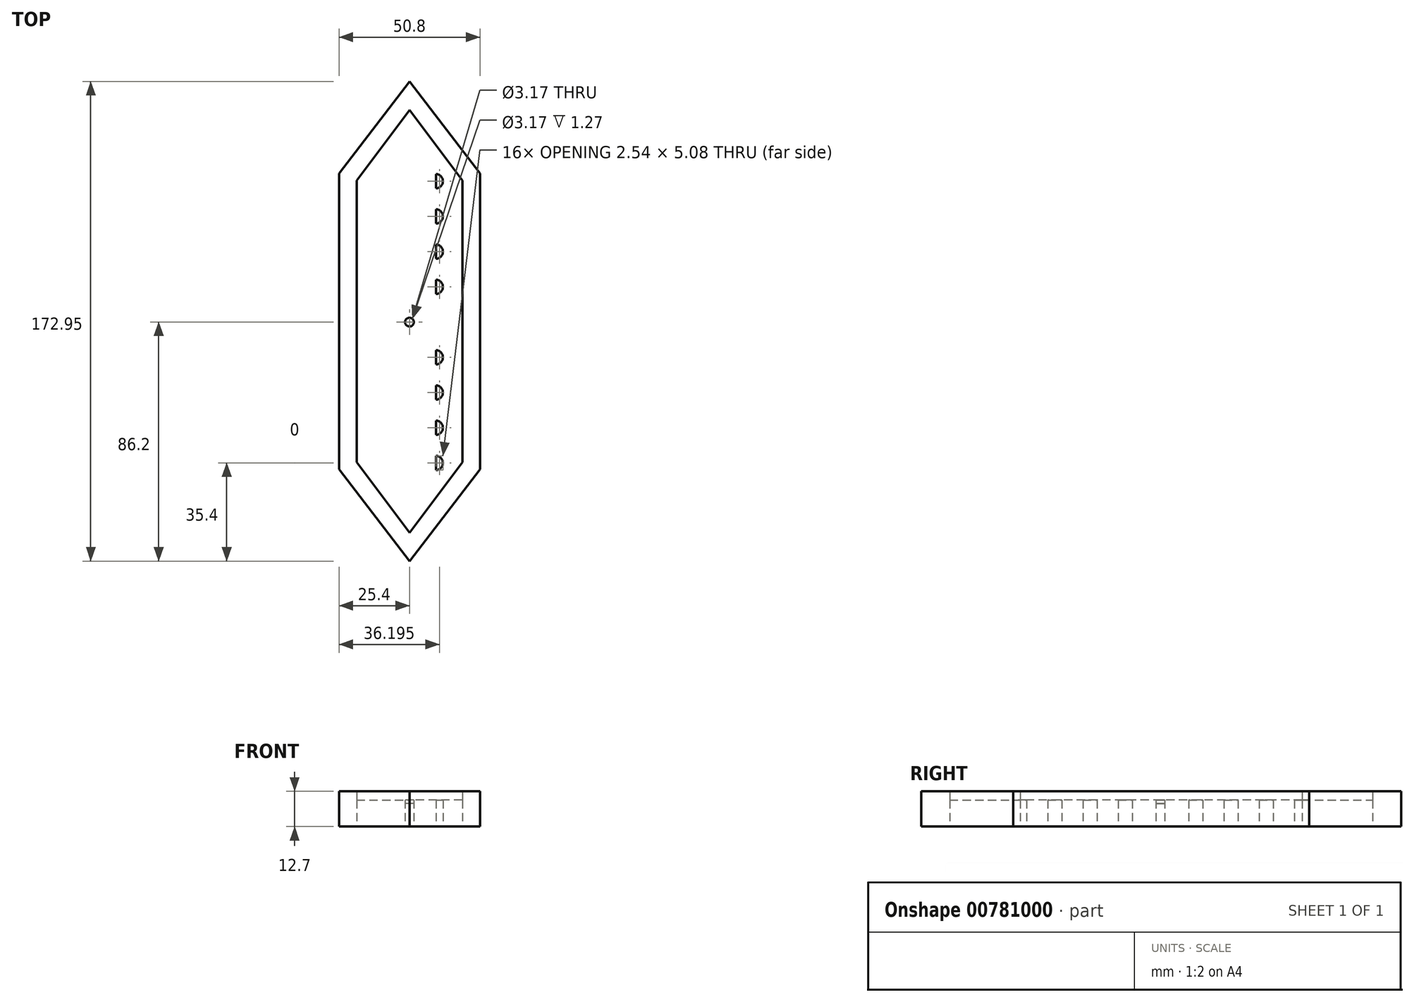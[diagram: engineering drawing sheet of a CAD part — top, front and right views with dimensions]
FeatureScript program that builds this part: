
annotation { "Feature Type Name" : "Feature", "Feature Type Description" : "" }
export const myFeature = defineFeature(function(context is Context, id is Id, definition is map)
    precondition{}
    {
        {
            var Q0;
            Q0=qCreatedBy(makeId("Top.planeOp"),FACE);
            var sketch = newSketch(context, id + "F0", { "sketchPlane" : qUnion([Q0])});
            skLineSegment(sketch, "E0", {"start": v(-25.4, 53.61) * mm, "end": v(-25.4, -53.07) * mm});
            skLineSegment(sketch, "E1", {"start": v(-25.4, -53.07) * mm, "end": v(0, -86.2) * mm});
            skLineSegment(sketch, "E2", {"start": v(0, -86.2) * mm, "end": v(25.4, -53.07) * mm});
            skLineSegment(sketch, "E3", {"start": v(25.4, -53.07) * mm, "end": v(25.4, 53.61) * mm});
            skLineSegment(sketch, "E4", {"start": v(25.4, 53.61) * mm, "end": v(0, 86.75) * mm});
            skLineSegment(sketch, "E5", {"start": v(0, 86.75) * mm, "end": v(-25.4, 53.61) * mm});
            skLineSegment(sketch, "E6", {"start": v(-19.05, 51.07) * mm, "end": v(0, 76.47) * mm});
            skLineSegment(sketch, "E7", {"start": v(0, 76.47) * mm, "end": v(19.05, 51.07) * mm});
            skLineSegment(sketch, "E8", {"start": v(19.05, 51.07) * mm, "end": v(19.05, -50.53) * mm});
            skLineSegment(sketch, "E9", {"start": v(19.05, -50.53) * mm, "end": v(0, -75.93) * mm});
            skLineSegment(sketch, "E10", {"start": v(0, -75.93) * mm, "end": v(-19.05, -50.53) * mm});
            skLineSegment(sketch, "E11", {"start": v(-19.05, 51.07) * mm, "end": v(-19.05, -50.53) * mm});
            skCircle(sketch, "E12", {"center": v(0, 0) * mm, "radius": 1.59 * mm});
            skCircle(sketch, "E13", {"center": v(0, 0) * mm, "radius": 3.18 * mm});
            skLineSegment(sketch, "E14.bottom", {"start": v(-2.38, 63.5) * mm, "end": v(2.38, 63.5) * mm});
            skLineSegment(sketch, "E14.top", {"start": v(-2.38, -63.5) * mm, "end": v(2.38, -63.5) * mm});
            skLineSegment(sketch, "E14.left", {"start": v(-2.38, 63.5) * mm, "end": v(-2.38, -63.5) * mm});
            skLineSegment(sketch, "E14.right", {"start": v(2.38, 63.5) * mm, "end": v(2.38, -63.5) * mm});
            skLineSegment(sketch, "E15.bottom", {"start": v(-9.52, 27.94) * mm, "end": v(9.52, 27.94) * mm});
            skLineSegment(sketch, "E15.top", {"start": v(-9.52, 22.86) * mm, "end": v(9.52, 22.86) * mm});
            skLineSegment(sketch, "E15.left", {"start": v(-9.52, 27.94) * mm, "end": v(-9.52, 22.86) * mm});
            skLineSegment(sketch, "E15.right", {"start": v(9.52, 27.94) * mm, "end": v(9.52, 22.86) * mm});
            skPoint(sketch, "E15.middle", {"position": v(0, 25.4) * mm});
            skLineSegment(sketch, "E16.bottom", {"start": v(-9.52, 40.64) * mm, "end": v(9.52, 40.64) * mm});
            skLineSegment(sketch, "E16.top", {"start": v(-9.52, 35.56) * mm, "end": v(9.52, 35.56) * mm});
            skLineSegment(sketch, "E16.left", {"start": v(-9.52, 40.64) * mm, "end": v(-9.52, 35.56) * mm});
            skLineSegment(sketch, "E16.right", {"start": v(9.52, 40.64) * mm, "end": v(9.52, 35.56) * mm});
            skPoint(sketch, "E16.middle", {"position": v(0, 38.1) * mm});
            skLineSegment(sketch, "E17.bottom", {"start": v(-9.52, 53.34) * mm, "end": v(9.53, 53.34) * mm});
            skLineSegment(sketch, "E17.top", {"start": v(-9.52, 48.26) * mm, "end": v(9.53, 48.26) * mm});
            skLineSegment(sketch, "E17.left", {"start": v(-9.52, 53.34) * mm, "end": v(-9.52, 48.26) * mm});
            skLineSegment(sketch, "E17.right", {"start": v(9.53, 53.34) * mm, "end": v(9.53, 48.26) * mm});
            skPoint(sketch, "E17.middle", {"position": v(0, 50.8) * mm});
            skLineSegment(sketch, "E18.bottom", {"start": v(-5.08, 65.4) * mm, "end": v(5.08, 65.4) * mm});
            skLineSegment(sketch, "E18.top", {"start": v(-5.08, 61.6) * mm, "end": v(5.08, 61.6) * mm});
            skLineSegment(sketch, "E18.left", {"start": v(-5.08, 65.4) * mm, "end": v(-5.08, 61.6) * mm});
            skLineSegment(sketch, "E18.right", {"start": v(5.08, 65.4) * mm, "end": v(5.08, 61.6) * mm});
            skPoint(sketch, "E18.middle", {"position": v(0, 63.5) * mm});
            skLineSegment(sketch, "E19.bottom", {"start": v(-9.52, 15.24) * mm, "end": v(9.52, 15.24) * mm});
            skLineSegment(sketch, "E19.top", {"start": v(-9.52, 10.16) * mm, "end": v(9.52, 10.16) * mm});
            skLineSegment(sketch, "E19.left", {"start": v(-9.52, 15.24) * mm, "end": v(-9.52, 10.16) * mm});
            skLineSegment(sketch, "E19.right", {"start": v(9.52, 15.24) * mm, "end": v(9.52, 10.16) * mm});
            skPoint(sketch, "E19.middle", {"position": v(0, 12.7) * mm});
            skLineSegment(sketch, "E20.bottom", {"start": v(-9.52, -10.16) * mm, "end": v(9.52, -10.16) * mm});
            skLineSegment(sketch, "E20.top", {"start": v(-9.52, -15.24) * mm, "end": v(9.52, -15.24) * mm});
            skLineSegment(sketch, "E20.left", {"start": v(-9.52, -10.16) * mm, "end": v(-9.52, -15.24) * mm});
            skLineSegment(sketch, "E20.right", {"start": v(9.52, -10.16) * mm, "end": v(9.52, -15.24) * mm});
            skPoint(sketch, "E20.middle", {"position": v(0, -12.7) * mm});
            skLineSegment(sketch, "E21.bottom", {"start": v(-9.52, -22.86) * mm, "end": v(9.52, -22.86) * mm});
            skLineSegment(sketch, "E21.top", {"start": v(-9.52, -27.94) * mm, "end": v(9.52, -27.94) * mm});
            skLineSegment(sketch, "E21.left", {"start": v(-9.52, -22.86) * mm, "end": v(-9.52, -27.94) * mm});
            skLineSegment(sketch, "E21.right", {"start": v(9.52, -22.86) * mm, "end": v(9.52, -27.94) * mm});
            skPoint(sketch, "E21.middle", {"position": v(0, -25.4) * mm});
            skLineSegment(sketch, "E22.bottom", {"start": v(-9.53, -35.56) * mm, "end": v(9.52, -35.56) * mm});
            skLineSegment(sketch, "E22.top", {"start": v(-9.53, -40.64) * mm, "end": v(9.52, -40.64) * mm});
            skLineSegment(sketch, "E22.left", {"start": v(-9.53, -35.56) * mm, "end": v(-9.53, -40.64) * mm});
            skLineSegment(sketch, "E22.right", {"start": v(9.52, -35.56) * mm, "end": v(9.52, -40.64) * mm});
            skPoint(sketch, "E22.middle", {"position": v(0, -38.1) * mm});
            skLineSegment(sketch, "E23.bottom", {"start": v(-9.53, -48.26) * mm, "end": v(9.52, -48.26) * mm});
            skLineSegment(sketch, "E23.top", {"start": v(-9.53, -53.34) * mm, "end": v(9.52, -53.34) * mm});
            skLineSegment(sketch, "E23.left", {"start": v(-9.53, -48.26) * mm, "end": v(-9.53, -53.34) * mm});
            skLineSegment(sketch, "E23.right", {"start": v(9.52, -48.26) * mm, "end": v(9.52, -53.34) * mm});
            skPoint(sketch, "E23.middle", {"position": v(0, -50.8) * mm});
            skLineSegment(sketch, "E24.bottom", {"start": v(-5.08, -61.6) * mm, "end": v(5.08, -61.6) * mm});
            skLineSegment(sketch, "E24.top", {"start": v(-5.08, -65.4) * mm, "end": v(5.08, -65.4) * mm});
            skLineSegment(sketch, "E24.left", {"start": v(-5.08, -61.6) * mm, "end": v(-5.08, -65.4) * mm});
            skLineSegment(sketch, "E24.right", {"start": v(5.08, -61.6) * mm, "end": v(5.08, -65.4) * mm});
            skPoint(sketch, "E24.middle", {"position": v(0, -63.5) * mm});
            skArc(sketch, "E25", {"start": v(-9.52, -10.16) * mm, "mid": v(-12.06, -12.7) * mm, "end": v(-9.52, -15.24) * mm});
            skArc(sketch, "E26", {"start": v(9.52, -10.16) * mm, "mid": v(12.06, -12.7) * mm, "end": v(9.52, -15.24) * mm});
            skArc(sketch, "E27", {"start": v(-9.52, -22.86) * mm, "mid": v(-12.06, -25.4) * mm, "end": v(-9.52, -27.94) * mm});
            skArc(sketch, "E28", {"start": v(9.52, -22.86) * mm, "mid": v(12.06, -25.4) * mm, "end": v(9.52, -27.94) * mm});
            skArc(sketch, "E29", {"start": v(-9.53, -35.56) * mm, "mid": v(-12.07, -38.1) * mm, "end": v(-9.53, -40.64) * mm});
            skArc(sketch, "E30", {"start": v(9.52, -35.56) * mm, "mid": v(12.06, -38.1) * mm, "end": v(9.52, -40.64) * mm});
            skArc(sketch, "E31", {"start": v(-9.53, -48.26) * mm, "mid": v(-12.07, -50.8) * mm, "end": v(-9.53, -53.34) * mm});
            skArc(sketch, "E32", {"start": v(9.52, -48.26) * mm, "mid": v(12.06, -50.8) * mm, "end": v(9.52, -53.34) * mm});
            skArc(sketch, "E33", {"start": v(-9.52, 15.24) * mm, "mid": v(-12.06, 12.7) * mm, "end": v(-9.52, 10.16) * mm});
            skArc(sketch, "E34", {"start": v(9.52, 15.24) * mm, "mid": v(12.06, 12.7) * mm, "end": v(9.52, 10.16) * mm});
            skArc(sketch, "E35", {"start": v(-9.52, 27.94) * mm, "mid": v(-12.06, 25.4) * mm, "end": v(-9.52, 22.86) * mm});
            skArc(sketch, "E36", {"start": v(9.52, 27.94) * mm, "mid": v(12.06, 25.4) * mm, "end": v(9.52, 22.86) * mm});
            skArc(sketch, "E37", {"start": v(-9.52, 40.64) * mm, "mid": v(-12.06, 38.1) * mm, "end": v(-9.52, 35.56) * mm});
            skArc(sketch, "E38", {"start": v(9.52, 40.64) * mm, "mid": v(12.06, 38.1) * mm, "end": v(9.52, 35.56) * mm});
            skArc(sketch, "E39", {"start": v(9.53, 53.34) * mm, "mid": v(12.07, 50.8) * mm, "end": v(9.53, 48.26) * mm});
            skArc(sketch, "E40", {"start": v(-9.52, 53.34) * mm, "mid": v(-12.06, 50.8) * mm, "end": v(-9.52, 48.26) * mm});
            skLineSegment(sketch, "E41", {"start": v(9.52, -50.8) * mm, "end": v(-9.53, -50.8) * mm});
            skLineSegment(sketch, "E42", {"start": v(9.52, -38.1) * mm, "end": v(-9.53, -38.1) * mm});
            skLineSegment(sketch, "E43", {"start": v(9.52, -25.4) * mm, "end": v(-9.52, -25.4) * mm});
            skLineSegment(sketch, "E44", {"start": v(9.52, -12.7) * mm, "end": v(-9.52, -12.7) * mm});
            skLineSegment(sketch, "E45", {"start": v(9.52, 12.7) * mm, "end": v(-9.52, 12.7) * mm});
            skLineSegment(sketch, "E46", {"start": v(9.52, 25.4) * mm, "end": v(-9.52, 25.4) * mm});
            skLineSegment(sketch, "E47", {"start": v(9.52, 38.1) * mm, "end": v(-9.52, 38.1) * mm});
            skLineSegment(sketch, "E48", {"start": v(9.53, 50.8) * mm, "end": v(-9.52, 50.8) * mm});
            skLineSegment(sketch, "E49", {"start": v(5.08, 63.5) * mm, "end": v(-5.08, 63.5) * mm});
            skLineSegment(sketch, "E50", {"start": v(5.08, -63.5) * mm, "end": v(-5.08, -63.5) * mm});
            skSolve(sketch);
        }
        {
            var Q0;
            Q0=makeQuery(id+"F0.imprint","IMPRINT",FACE,{"disambiguationData":[TD([[makeQuery(id+"F0.imprint","IMPRINT",EDGE,{"derivedFrom":sQuery(id+"F0.wireOp",EDGE,"E6")}),-1.0]])]});
            extrude(context, id + "F1", {"entities" : qUnion([Q0]), "depth" : 6.35 * mm, "offsetDistance" : 25.4 * mm});
        }
        {
            var Q0;
            Q0=makeQuery(id+"F0.imprint","IMPRINT",FACE,{"disambiguationData":[TD([[makeQuery(id+"F0.imprint","IMPRINT",EDGE,{"derivedFrom":sQuery(id+"F0.wireOp",EDGE,"E0")}),1.0]])]});
            extrude(context, id + "F2", {"entities" : qUnion([Q0]), "operationType" : NewBodyOperationType.ADD, "depth" : 12.7 * mm, "offsetDistance" : 25.4 * mm});
        }
        {
            var Q0;
            Q0=makeQuery(id+"F0.imprint","IMPRINT",FACE,{"disambiguationData":[TD([[makeQuery(id+"F0.imprint","IMPRINT",EDGE,{"derivedFrom":sQuery(id+"F0.wireOp",EDGE,"E12")}),1.0]])]});
            extrude(context, id + "F3", {"entities" : qUnion([Q0]), "operationType" : NewBodyOperationType.ADD, "depth" : 8.25 * mm, "offsetDistance" : 25.4 * mm});
        }
        {
            var Q0;
            {var subQ4=sQuery(id+"F0.wireOp",EDGE,"E24.top");Q0=makeQuery(id+"F0.imprint","IMPRINT",FACE,{"disambiguationData":[TD([[makeQuery(id+"F0.imprint","IMPRINT",EDGE,{"derivedFrom":subQ4}),1.0]])]});}
            var Q1;
            {var subQ0=sQuery(id+"F0.wireOp",EDGE,"E50");var subQ1=sQuery(id+"F0.wireOp",EDGE,"E14.left");var subQ2=makeQuery(id+"F0.imprint","INTERSECT",VERTEX,{"derivedFrom":[subQ1,subQ0]});Q1=makeQuery(id+"F0.imprint","IMPRINT",FACE,{"disambiguationData":[TD([[makeQuery(id+"F0.imprint","IMPRINT",EDGE,{"disambiguationData":[TD([[subQ2,1.0]])],"derivedFrom":subQ1}),-1.0]])]});}
            var Q2;
            {var subQ0=sQuery(id+"F0.wireOp",EDGE,"E50");var subQ1=sQuery(id+"F0.wireOp",EDGE,"E14.left");var subQ2=makeQuery(id+"F0.imprint","INTERSECT",VERTEX,{"derivedFrom":[subQ1,subQ0]});Q2=makeQuery(id+"F0.imprint","IMPRINT",FACE,{"disambiguationData":[TD([[makeQuery(id+"F0.imprint","IMPRINT",EDGE,{"disambiguationData":[TD([[subQ2,1.0]])],"derivedFrom":subQ1}),1.0]])]});}
            var Q3;
            {var subQ0=sQuery(id+"F0.wireOp",EDGE,"E50");var subQ1=sQuery(id+"F0.wireOp",EDGE,"E14.right");var subQ2=makeQuery(id+"F0.imprint","INTERSECT",VERTEX,{"derivedFrom":[subQ1,subQ0]});Q3=makeQuery(id+"F0.imprint","IMPRINT",FACE,{"disambiguationData":[TD([[makeQuery(id+"F0.imprint","IMPRINT",EDGE,{"disambiguationData":[TD([[subQ2,1.0]])],"derivedFrom":subQ1}),1.0]])]});}
            var Q4;
            {var subQ0=sQuery(id+"F0.wireOp",EDGE,"E23.top");var subQ1=sQuery(id+"F0.wireOp",EDGE,"E14.left");var subQ2=makeQuery(id+"F0.imprint","INTERSECT",VERTEX,{"derivedFrom":[subQ1,subQ0]});Q4=makeQuery(id+"F0.imprint","IMPRINT",FACE,{"disambiguationData":[TD([[makeQuery(id+"F0.imprint","IMPRINT",EDGE,{"disambiguationData":[TD([[subQ2,-1.0]])],"derivedFrom":subQ1}),1.0]])]});}
            var Q5;
            {var subQ0=sQuery(id+"F0.wireOp",EDGE,"E31");Q5=makeQuery(id+"F0.imprint","IMPRINT",FACE,{"disambiguationData":[TD([[makeQuery(id+"F0.imprint","IMPRINT",EDGE,{"derivedFrom":subQ0}),1.0]])]});}
            var Q6;
            {var subQ0=sQuery(id+"F0.wireOp",EDGE,"E23.bottom");var subQ1=sQuery(id+"F0.wireOp",EDGE,"E14.left");var subQ2=makeQuery(id+"F0.imprint","INTERSECT",VERTEX,{"derivedFrom":[subQ1,subQ0]});Q6=makeQuery(id+"F0.imprint","IMPRINT",FACE,{"disambiguationData":[TD([[makeQuery(id+"F0.imprint","IMPRINT",EDGE,{"disambiguationData":[TD([[subQ2,-1.0]])],"derivedFrom":subQ1}),-1.0]])]});}
            var Q7;
            {var subQ0=sQuery(id+"F0.wireOp",EDGE,"E41");var subQ1=sQuery(id+"F0.wireOp",EDGE,"E14.left");var subQ2=makeQuery(id+"F0.imprint","INTERSECT",VERTEX,{"derivedFrom":[subQ1,subQ0]});Q7=makeQuery(id+"F0.imprint","IMPRINT",FACE,{"disambiguationData":[TD([[makeQuery(id+"F0.imprint","IMPRINT",EDGE,{"disambiguationData":[TD([[subQ2,-1.0]])],"derivedFrom":subQ1}),-1.0]])]});}
            var Q8;
            {var subQ0=sQuery(id+"F0.wireOp",EDGE,"E41");var subQ1=sQuery(id+"F0.wireOp",EDGE,"E14.left");var subQ2=makeQuery(id+"F0.imprint","INTERSECT",VERTEX,{"derivedFrom":[subQ1,subQ0]});Q8=makeQuery(id+"F0.imprint","IMPRINT",FACE,{"disambiguationData":[TD([[makeQuery(id+"F0.imprint","IMPRINT",EDGE,{"disambiguationData":[TD([[subQ2,-1.0]])],"derivedFrom":subQ1}),1.0]])]});}
            var Q9;
            {var subQ0=sQuery(id+"F0.wireOp",EDGE,"E23.bottom");var subQ1=sQuery(id+"F0.wireOp",EDGE,"E14.left");var subQ2=makeQuery(id+"F0.imprint","INTERSECT",VERTEX,{"derivedFrom":[subQ1,subQ0]});Q9=makeQuery(id+"F0.imprint","IMPRINT",FACE,{"disambiguationData":[TD([[makeQuery(id+"F0.imprint","IMPRINT",EDGE,{"disambiguationData":[TD([[subQ2,-1.0]])],"derivedFrom":subQ1}),1.0]])]});}
            var Q10;
            {var subQ0=sQuery(id+"F0.wireOp",EDGE,"E41");var subQ1=sQuery(id+"F0.wireOp",EDGE,"E14.right");var subQ2=makeQuery(id+"F0.imprint","INTERSECT",VERTEX,{"derivedFrom":[subQ1,subQ0]});Q10=makeQuery(id+"F0.imprint","IMPRINT",FACE,{"disambiguationData":[TD([[makeQuery(id+"F0.imprint","IMPRINT",EDGE,{"disambiguationData":[TD([[subQ2,-1.0]])],"derivedFrom":subQ1}),1.0]])]});}
            var Q11;
            {var subQ0=sQuery(id+"F0.wireOp",EDGE,"E23.bottom");var subQ1=sQuery(id+"F0.wireOp",EDGE,"E14.right");var subQ2=makeQuery(id+"F0.imprint","INTERSECT",VERTEX,{"derivedFrom":[subQ1,subQ0]});Q11=makeQuery(id+"F0.imprint","IMPRINT",FACE,{"disambiguationData":[TD([[makeQuery(id+"F0.imprint","IMPRINT",EDGE,{"disambiguationData":[TD([[subQ2,-1.0]])],"derivedFrom":subQ1}),1.0]])]});}
            var Q12;
            {var subQ0=sQuery(id+"F0.wireOp",EDGE,"E32");Q12=makeQuery(id+"F0.imprint","IMPRINT",FACE,{"disambiguationData":[TD([[makeQuery(id+"F0.imprint","IMPRINT",EDGE,{"derivedFrom":subQ0}),-1.0]])]});}
            var Q13;
            {var subQ0=sQuery(id+"F0.wireOp",EDGE,"E29");Q13=makeQuery(id+"F0.imprint","IMPRINT",FACE,{"disambiguationData":[TD([[makeQuery(id+"F0.imprint","IMPRINT",EDGE,{"derivedFrom":subQ0}),1.0]])]});}
            var Q14;
            {var subQ0=sQuery(id+"F0.wireOp",EDGE,"E22.bottom");var subQ1=sQuery(id+"F0.wireOp",EDGE,"E14.left");var subQ2=makeQuery(id+"F0.imprint","INTERSECT",VERTEX,{"derivedFrom":[subQ1,subQ0]});Q14=makeQuery(id+"F0.imprint","IMPRINT",FACE,{"disambiguationData":[TD([[makeQuery(id+"F0.imprint","IMPRINT",EDGE,{"disambiguationData":[TD([[subQ2,-1.0]])],"derivedFrom":subQ1}),-1.0]])]});}
            var Q15;
            {var subQ0=sQuery(id+"F0.wireOp",EDGE,"E42");var subQ1=sQuery(id+"F0.wireOp",EDGE,"E14.left");var subQ2=makeQuery(id+"F0.imprint","INTERSECT",VERTEX,{"derivedFrom":[subQ1,subQ0]});Q15=makeQuery(id+"F0.imprint","IMPRINT",FACE,{"disambiguationData":[TD([[makeQuery(id+"F0.imprint","IMPRINT",EDGE,{"disambiguationData":[TD([[subQ2,-1.0]])],"derivedFrom":subQ1}),-1.0]])]});}
            var Q16;
            {var subQ0=sQuery(id+"F0.wireOp",EDGE,"E22.top");var subQ1=sQuery(id+"F0.wireOp",EDGE,"E14.left");var subQ2=makeQuery(id+"F0.imprint","INTERSECT",VERTEX,{"derivedFrom":[subQ1,subQ0]});Q16=makeQuery(id+"F0.imprint","IMPRINT",FACE,{"disambiguationData":[TD([[makeQuery(id+"F0.imprint","IMPRINT",EDGE,{"disambiguationData":[TD([[subQ2,-1.0]])],"derivedFrom":subQ1}),1.0]])]});}
            var Q17;
            {var subQ0=sQuery(id+"F0.wireOp",EDGE,"E42");var subQ1=sQuery(id+"F0.wireOp",EDGE,"E14.left");var subQ2=makeQuery(id+"F0.imprint","INTERSECT",VERTEX,{"derivedFrom":[subQ1,subQ0]});Q17=makeQuery(id+"F0.imprint","IMPRINT",FACE,{"disambiguationData":[TD([[makeQuery(id+"F0.imprint","IMPRINT",EDGE,{"disambiguationData":[TD([[subQ2,-1.0]])],"derivedFrom":subQ1}),1.0]])]});}
            var Q18;
            {var subQ0=sQuery(id+"F0.wireOp",EDGE,"E22.bottom");var subQ1=sQuery(id+"F0.wireOp",EDGE,"E14.left");var subQ2=makeQuery(id+"F0.imprint","INTERSECT",VERTEX,{"derivedFrom":[subQ1,subQ0]});Q18=makeQuery(id+"F0.imprint","IMPRINT",FACE,{"disambiguationData":[TD([[makeQuery(id+"F0.imprint","IMPRINT",EDGE,{"disambiguationData":[TD([[subQ2,-1.0]])],"derivedFrom":subQ1}),1.0]])]});}
            var Q19;
            {var subQ0=sQuery(id+"F0.wireOp",EDGE,"E42");var subQ1=sQuery(id+"F0.wireOp",EDGE,"E14.right");var subQ2=makeQuery(id+"F0.imprint","INTERSECT",VERTEX,{"derivedFrom":[subQ1,subQ0]});Q19=makeQuery(id+"F0.imprint","IMPRINT",FACE,{"disambiguationData":[TD([[makeQuery(id+"F0.imprint","IMPRINT",EDGE,{"disambiguationData":[TD([[subQ2,-1.0]])],"derivedFrom":subQ1}),1.0]])]});}
            var Q20;
            {var subQ0=sQuery(id+"F0.wireOp",EDGE,"E22.bottom");var subQ1=sQuery(id+"F0.wireOp",EDGE,"E14.right");var subQ2=makeQuery(id+"F0.imprint","INTERSECT",VERTEX,{"derivedFrom":[subQ1,subQ0]});Q20=makeQuery(id+"F0.imprint","IMPRINT",FACE,{"disambiguationData":[TD([[makeQuery(id+"F0.imprint","IMPRINT",EDGE,{"disambiguationData":[TD([[subQ2,-1.0]])],"derivedFrom":subQ1}),1.0]])]});}
            var Q21;
            {var subQ0=sQuery(id+"F0.wireOp",EDGE,"E30");Q21=makeQuery(id+"F0.imprint","IMPRINT",FACE,{"disambiguationData":[TD([[makeQuery(id+"F0.imprint","IMPRINT",EDGE,{"derivedFrom":subQ0}),-1.0]])]});}
            var Q22;
            {var subQ0=sQuery(id+"F0.wireOp",EDGE,"E27");Q22=makeQuery(id+"F0.imprint","IMPRINT",FACE,{"disambiguationData":[TD([[makeQuery(id+"F0.imprint","IMPRINT",EDGE,{"derivedFrom":subQ0}),1.0]])]});}
            var Q23;
            {var subQ0=sQuery(id+"F0.wireOp",EDGE,"E43");var subQ1=sQuery(id+"F0.wireOp",EDGE,"E14.left");var subQ2=makeQuery(id+"F0.imprint","INTERSECT",VERTEX,{"derivedFrom":[subQ1,subQ0]});Q23=makeQuery(id+"F0.imprint","IMPRINT",FACE,{"disambiguationData":[TD([[makeQuery(id+"F0.imprint","IMPRINT",EDGE,{"disambiguationData":[TD([[subQ2,-1.0]])],"derivedFrom":subQ1}),-1.0]])]});}
            var Q24;
            {var subQ0=sQuery(id+"F0.wireOp",EDGE,"E21.bottom");var subQ1=sQuery(id+"F0.wireOp",EDGE,"E14.left");var subQ2=makeQuery(id+"F0.imprint","INTERSECT",VERTEX,{"derivedFrom":[subQ1,subQ0]});Q24=makeQuery(id+"F0.imprint","IMPRINT",FACE,{"disambiguationData":[TD([[makeQuery(id+"F0.imprint","IMPRINT",EDGE,{"disambiguationData":[TD([[subQ2,-1.0]])],"derivedFrom":subQ1}),-1.0]])]});}
            var Q25;
            {var subQ0=sQuery(id+"F0.wireOp",EDGE,"E21.top");var subQ1=sQuery(id+"F0.wireOp",EDGE,"E14.left");var subQ2=makeQuery(id+"F0.imprint","INTERSECT",VERTEX,{"derivedFrom":[subQ1,subQ0]});Q25=makeQuery(id+"F0.imprint","IMPRINT",FACE,{"disambiguationData":[TD([[makeQuery(id+"F0.imprint","IMPRINT",EDGE,{"disambiguationData":[TD([[subQ2,-1.0]])],"derivedFrom":subQ1}),1.0]])]});}
            var Q26;
            {var subQ0=sQuery(id+"F0.wireOp",EDGE,"E43");var subQ1=sQuery(id+"F0.wireOp",EDGE,"E14.left");var subQ2=makeQuery(id+"F0.imprint","INTERSECT",VERTEX,{"derivedFrom":[subQ1,subQ0]});Q26=makeQuery(id+"F0.imprint","IMPRINT",FACE,{"disambiguationData":[TD([[makeQuery(id+"F0.imprint","IMPRINT",EDGE,{"disambiguationData":[TD([[subQ2,-1.0]])],"derivedFrom":subQ1}),1.0]])]});}
            var Q27;
            {var subQ0=sQuery(id+"F0.wireOp",EDGE,"E21.bottom");var subQ1=sQuery(id+"F0.wireOp",EDGE,"E14.left");var subQ2=makeQuery(id+"F0.imprint","INTERSECT",VERTEX,{"derivedFrom":[subQ1,subQ0]});Q27=makeQuery(id+"F0.imprint","IMPRINT",FACE,{"disambiguationData":[TD([[makeQuery(id+"F0.imprint","IMPRINT",EDGE,{"disambiguationData":[TD([[subQ2,-1.0]])],"derivedFrom":subQ1}),1.0]])]});}
            var Q28;
            {var subQ0=sQuery(id+"F0.wireOp",EDGE,"E43");var subQ1=sQuery(id+"F0.wireOp",EDGE,"E14.right");var subQ2=makeQuery(id+"F0.imprint","INTERSECT",VERTEX,{"derivedFrom":[subQ1,subQ0]});Q28=makeQuery(id+"F0.imprint","IMPRINT",FACE,{"disambiguationData":[TD([[makeQuery(id+"F0.imprint","IMPRINT",EDGE,{"disambiguationData":[TD([[subQ2,-1.0]])],"derivedFrom":subQ1}),1.0]])]});}
            var Q29;
            {var subQ0=sQuery(id+"F0.wireOp",EDGE,"E21.bottom");var subQ1=sQuery(id+"F0.wireOp",EDGE,"E14.right");var subQ2=makeQuery(id+"F0.imprint","INTERSECT",VERTEX,{"derivedFrom":[subQ1,subQ0]});Q29=makeQuery(id+"F0.imprint","IMPRINT",FACE,{"disambiguationData":[TD([[makeQuery(id+"F0.imprint","IMPRINT",EDGE,{"disambiguationData":[TD([[subQ2,-1.0]])],"derivedFrom":subQ1}),1.0]])]});}
            var Q30;
            {var subQ0=sQuery(id+"F0.wireOp",EDGE,"E28");Q30=makeQuery(id+"F0.imprint","IMPRINT",FACE,{"disambiguationData":[TD([[makeQuery(id+"F0.imprint","IMPRINT",EDGE,{"derivedFrom":subQ0}),-1.0]])]});}
            var Q31;
            {var subQ0=sQuery(id+"F0.wireOp",EDGE,"E20.top");var subQ1=sQuery(id+"F0.wireOp",EDGE,"E14.left");var subQ2=makeQuery(id+"F0.imprint","INTERSECT",VERTEX,{"derivedFrom":[subQ1,subQ0]});Q31=makeQuery(id+"F0.imprint","IMPRINT",FACE,{"disambiguationData":[TD([[makeQuery(id+"F0.imprint","IMPRINT",EDGE,{"disambiguationData":[TD([[subQ2,-1.0]])],"derivedFrom":subQ1}),1.0]])]});}
            var Q32;
            {var subQ0=sQuery(id+"F0.wireOp",EDGE,"E44");var subQ1=sQuery(id+"F0.wireOp",EDGE,"E14.left");var subQ2=makeQuery(id+"F0.imprint","INTERSECT",VERTEX,{"derivedFrom":[subQ1,subQ0]});Q32=makeQuery(id+"F0.imprint","IMPRINT",FACE,{"disambiguationData":[TD([[makeQuery(id+"F0.imprint","IMPRINT",EDGE,{"disambiguationData":[TD([[subQ2,-1.0]])],"derivedFrom":subQ1}),-1.0]])]});}
            var Q33;
            {var subQ0=sQuery(id+"F0.wireOp",EDGE,"E25");Q33=makeQuery(id+"F0.imprint","IMPRINT",FACE,{"disambiguationData":[TD([[makeQuery(id+"F0.imprint","IMPRINT",EDGE,{"derivedFrom":subQ0}),1.0]])]});}
            var Q34;
            {var subQ0=sQuery(id+"F0.wireOp",EDGE,"E20.bottom");var subQ1=sQuery(id+"F0.wireOp",EDGE,"E14.left");var subQ2=makeQuery(id+"F0.imprint","INTERSECT",VERTEX,{"derivedFrom":[subQ1,subQ0]});Q34=makeQuery(id+"F0.imprint","IMPRINT",FACE,{"disambiguationData":[TD([[makeQuery(id+"F0.imprint","IMPRINT",EDGE,{"disambiguationData":[TD([[subQ2,-1.0]])],"derivedFrom":subQ1}),-1.0]])]});}
            var Q35;
            {var subQ0=sQuery(id+"F0.wireOp",EDGE,"E20.bottom");var subQ1=sQuery(id+"F0.wireOp",EDGE,"E14.left");var subQ2=makeQuery(id+"F0.imprint","INTERSECT",VERTEX,{"derivedFrom":[subQ1,subQ0]});Q35=makeQuery(id+"F0.imprint","IMPRINT",FACE,{"disambiguationData":[TD([[makeQuery(id+"F0.imprint","IMPRINT",EDGE,{"disambiguationData":[TD([[subQ2,-1.0]])],"derivedFrom":subQ1}),1.0]])]});}
            var Q36;
            {var subQ0=sQuery(id+"F0.wireOp",EDGE,"E44");var subQ1=sQuery(id+"F0.wireOp",EDGE,"E14.right");var subQ2=makeQuery(id+"F0.imprint","INTERSECT",VERTEX,{"derivedFrom":[subQ1,subQ0]});Q36=makeQuery(id+"F0.imprint","IMPRINT",FACE,{"disambiguationData":[TD([[makeQuery(id+"F0.imprint","IMPRINT",EDGE,{"disambiguationData":[TD([[subQ2,-1.0]])],"derivedFrom":subQ1}),1.0]])]});}
            var Q37;
            {var subQ0=sQuery(id+"F0.wireOp",EDGE,"E26");Q37=makeQuery(id+"F0.imprint","IMPRINT",FACE,{"disambiguationData":[TD([[makeQuery(id+"F0.imprint","IMPRINT",EDGE,{"derivedFrom":subQ0}),-1.0]])]});}
            var Q38;
            {var subQ0=sQuery(id+"F0.wireOp",EDGE,"E44");var subQ1=sQuery(id+"F0.wireOp",EDGE,"E14.left");var subQ2=makeQuery(id+"F0.imprint","INTERSECT",VERTEX,{"derivedFrom":[subQ1,subQ0]});Q38=makeQuery(id+"F0.imprint","IMPRINT",FACE,{"disambiguationData":[TD([[makeQuery(id+"F0.imprint","IMPRINT",EDGE,{"disambiguationData":[TD([[subQ2,-1.0]])],"derivedFrom":subQ1}),1.0]])]});}
            var Q39;
            {var subQ0=sQuery(id+"F0.wireOp",EDGE,"E14.left");var subQ1=sQuery(id+"F0.wireOp",EDGE,"E13");var subQ2=makeQuery(id+"F0.imprint","INTERSECT",VERTEX,{"disambiguationData":[OD(1.0)],"derivedFrom":[subQ1,subQ0]});Q39=makeQuery(id+"F0.imprint","IMPRINT",FACE,{"disambiguationData":[TD([[makeQuery(id+"F0.imprint","IMPRINT",EDGE,{"disambiguationData":[TD([[subQ2,-1.0]])],"derivedFrom":subQ1}),-1.0]])]});}
            var Q40;
            {var subQ0=sQuery(id+"F0.wireOp",EDGE,"E14.left");var subQ1=sQuery(id+"F0.wireOp",EDGE,"E13");var subQ2=makeQuery(id+"F0.imprint","INTERSECT",VERTEX,{"disambiguationData":[OD(0.0)],"derivedFrom":[subQ1,subQ0]});Q40=makeQuery(id+"F0.imprint","IMPRINT",FACE,{"disambiguationData":[TD([[makeQuery(id+"F0.imprint","IMPRINT",EDGE,{"disambiguationData":[TD([[subQ2,1.0]])],"derivedFrom":subQ1}),-1.0]])]});}
            var Q41;
            Q41=makeQuery(id+"F0.imprint","IMPRINT",FACE,{"disambiguationData":[TD([[makeQuery(id+"F0.imprint","IMPRINT",EDGE,{"derivedFrom":sQuery(id+"F0.wireOp",EDGE,"E12")}),-1.0]])]});
            var Q42;
            {var subQ0=sQuery(id+"F0.wireOp",EDGE,"E14.right");var subQ1=sQuery(id+"F0.wireOp",EDGE,"E13");var subQ2=makeQuery(id+"F0.imprint","INTERSECT",VERTEX,{"disambiguationData":[OD(0.0)],"derivedFrom":[subQ1,subQ0]});Q42=makeQuery(id+"F0.imprint","IMPRINT",FACE,{"disambiguationData":[TD([[makeQuery(id+"F0.imprint","IMPRINT",EDGE,{"disambiguationData":[TD([[subQ2,1.0]])],"derivedFrom":subQ1}),1.0]])]});}
            var Q43;
            {var subQ0=sQuery(id+"F0.wireOp",EDGE,"E14.left");var subQ1=sQuery(id+"F0.wireOp",EDGE,"E13");var subQ2=makeQuery(id+"F0.imprint","INTERSECT",VERTEX,{"disambiguationData":[OD(0.0)],"derivedFrom":[subQ1,subQ0]});Q43=makeQuery(id+"F0.imprint","IMPRINT",FACE,{"disambiguationData":[TD([[makeQuery(id+"F0.imprint","IMPRINT",EDGE,{"disambiguationData":[TD([[subQ2,-1.0]])],"derivedFrom":subQ1}),1.0]])]});}
            var Q44;
            {var subQ0=sQuery(id+"F0.wireOp",EDGE,"E45");var subQ1=sQuery(id+"F0.wireOp",EDGE,"E14.left");var subQ2=makeQuery(id+"F0.imprint","INTERSECT",VERTEX,{"derivedFrom":[subQ1,subQ0]});Q44=makeQuery(id+"F0.imprint","IMPRINT",FACE,{"disambiguationData":[TD([[makeQuery(id+"F0.imprint","IMPRINT",EDGE,{"disambiguationData":[TD([[subQ2,-1.0]])],"derivedFrom":subQ1}),1.0]])]});}
            var Q45;
            {var subQ0=sQuery(id+"F0.wireOp",EDGE,"E45");var subQ1=sQuery(id+"F0.wireOp",EDGE,"E14.left");var subQ2=makeQuery(id+"F0.imprint","INTERSECT",VERTEX,{"derivedFrom":[subQ1,subQ0]});Q45=makeQuery(id+"F0.imprint","IMPRINT",FACE,{"disambiguationData":[TD([[makeQuery(id+"F0.imprint","IMPRINT",EDGE,{"disambiguationData":[TD([[subQ2,-1.0]])],"derivedFrom":subQ1}),-1.0]])]});}
            var Q46;
            {var subQ0=sQuery(id+"F0.wireOp",EDGE,"E33");Q46=makeQuery(id+"F0.imprint","IMPRINT",FACE,{"disambiguationData":[TD([[makeQuery(id+"F0.imprint","IMPRINT",EDGE,{"derivedFrom":subQ0}),1.0]])]});}
            var Q47;
            {var subQ0=sQuery(id+"F0.wireOp",EDGE,"E19.bottom");var subQ1=sQuery(id+"F0.wireOp",EDGE,"E14.left");var subQ2=makeQuery(id+"F0.imprint","INTERSECT",VERTEX,{"derivedFrom":[subQ1,subQ0]});Q47=makeQuery(id+"F0.imprint","IMPRINT",FACE,{"disambiguationData":[TD([[makeQuery(id+"F0.imprint","IMPRINT",EDGE,{"disambiguationData":[TD([[subQ2,-1.0]])],"derivedFrom":subQ1}),-1.0]])]});}
            var Q48;
            {var subQ0=sQuery(id+"F0.wireOp",EDGE,"E19.bottom");var subQ1=sQuery(id+"F0.wireOp",EDGE,"E14.left");var subQ2=makeQuery(id+"F0.imprint","INTERSECT",VERTEX,{"derivedFrom":[subQ1,subQ0]});Q48=makeQuery(id+"F0.imprint","IMPRINT",FACE,{"disambiguationData":[TD([[makeQuery(id+"F0.imprint","IMPRINT",EDGE,{"disambiguationData":[TD([[subQ2,-1.0]])],"derivedFrom":subQ1}),1.0]])]});}
            var Q49;
            {var subQ0=sQuery(id+"F0.wireOp",EDGE,"E19.bottom");var subQ1=sQuery(id+"F0.wireOp",EDGE,"E14.right");var subQ2=makeQuery(id+"F0.imprint","INTERSECT",VERTEX,{"derivedFrom":[subQ1,subQ0]});Q49=makeQuery(id+"F0.imprint","IMPRINT",FACE,{"disambiguationData":[TD([[makeQuery(id+"F0.imprint","IMPRINT",EDGE,{"disambiguationData":[TD([[subQ2,-1.0]])],"derivedFrom":subQ1}),1.0]])]});}
            var Q50;
            {var subQ0=sQuery(id+"F0.wireOp",EDGE,"E45");var subQ1=sQuery(id+"F0.wireOp",EDGE,"E14.right");var subQ2=makeQuery(id+"F0.imprint","INTERSECT",VERTEX,{"derivedFrom":[subQ1,subQ0]});Q50=makeQuery(id+"F0.imprint","IMPRINT",FACE,{"disambiguationData":[TD([[makeQuery(id+"F0.imprint","IMPRINT",EDGE,{"disambiguationData":[TD([[subQ2,-1.0]])],"derivedFrom":subQ1}),1.0]])]});}
            var Q51;
            {var subQ0=sQuery(id+"F0.wireOp",EDGE,"E34");Q51=makeQuery(id+"F0.imprint","IMPRINT",FACE,{"disambiguationData":[TD([[makeQuery(id+"F0.imprint","IMPRINT",EDGE,{"derivedFrom":subQ0}),-1.0]])]});}
            var Q52;
            {var subQ0=sQuery(id+"F0.wireOp",EDGE,"E15.top");var subQ1=sQuery(id+"F0.wireOp",EDGE,"E14.left");var subQ2=makeQuery(id+"F0.imprint","INTERSECT",VERTEX,{"derivedFrom":[subQ1,subQ0]});Q52=makeQuery(id+"F0.imprint","IMPRINT",FACE,{"disambiguationData":[TD([[makeQuery(id+"F0.imprint","IMPRINT",EDGE,{"disambiguationData":[TD([[subQ2,-1.0]])],"derivedFrom":subQ1}),1.0]])]});}
            var Q53;
            {var subQ0=sQuery(id+"F0.wireOp",EDGE,"E46");var subQ1=sQuery(id+"F0.wireOp",EDGE,"E14.left");var subQ2=makeQuery(id+"F0.imprint","INTERSECT",VERTEX,{"derivedFrom":[subQ1,subQ0]});Q53=makeQuery(id+"F0.imprint","IMPRINT",FACE,{"disambiguationData":[TD([[makeQuery(id+"F0.imprint","IMPRINT",EDGE,{"disambiguationData":[TD([[subQ2,-1.0]])],"derivedFrom":subQ1}),-1.0]])]});}
            var Q54;
            {var subQ0=sQuery(id+"F0.wireOp",EDGE,"E35");Q54=makeQuery(id+"F0.imprint","IMPRINT",FACE,{"disambiguationData":[TD([[makeQuery(id+"F0.imprint","IMPRINT",EDGE,{"derivedFrom":subQ0}),1.0]])]});}
            var Q55;
            {var subQ0=sQuery(id+"F0.wireOp",EDGE,"E15.bottom");var subQ1=sQuery(id+"F0.wireOp",EDGE,"E14.left");var subQ2=makeQuery(id+"F0.imprint","INTERSECT",VERTEX,{"derivedFrom":[subQ1,subQ0]});Q55=makeQuery(id+"F0.imprint","IMPRINT",FACE,{"disambiguationData":[TD([[makeQuery(id+"F0.imprint","IMPRINT",EDGE,{"disambiguationData":[TD([[subQ2,-1.0]])],"derivedFrom":subQ1}),-1.0]])]});}
            var Q56;
            {var subQ0=sQuery(id+"F0.wireOp",EDGE,"E15.bottom");var subQ1=sQuery(id+"F0.wireOp",EDGE,"E14.left");var subQ2=makeQuery(id+"F0.imprint","INTERSECT",VERTEX,{"derivedFrom":[subQ1,subQ0]});Q56=makeQuery(id+"F0.imprint","IMPRINT",FACE,{"disambiguationData":[TD([[makeQuery(id+"F0.imprint","IMPRINT",EDGE,{"disambiguationData":[TD([[subQ2,-1.0]])],"derivedFrom":subQ1}),1.0]])]});}
            var Q57;
            {var subQ0=sQuery(id+"F0.wireOp",EDGE,"E46");var subQ1=sQuery(id+"F0.wireOp",EDGE,"E14.left");var subQ2=makeQuery(id+"F0.imprint","INTERSECT",VERTEX,{"derivedFrom":[subQ1,subQ0]});Q57=makeQuery(id+"F0.imprint","IMPRINT",FACE,{"disambiguationData":[TD([[makeQuery(id+"F0.imprint","IMPRINT",EDGE,{"disambiguationData":[TD([[subQ2,-1.0]])],"derivedFrom":subQ1}),1.0]])]});}
            var Q58;
            {var subQ0=sQuery(id+"F0.wireOp",EDGE,"E46");var subQ1=sQuery(id+"F0.wireOp",EDGE,"E14.right");var subQ2=makeQuery(id+"F0.imprint","INTERSECT",VERTEX,{"derivedFrom":[subQ1,subQ0]});Q58=makeQuery(id+"F0.imprint","IMPRINT",FACE,{"disambiguationData":[TD([[makeQuery(id+"F0.imprint","IMPRINT",EDGE,{"disambiguationData":[TD([[subQ2,-1.0]])],"derivedFrom":subQ1}),1.0]])]});}
            var Q59;
            {var subQ0=sQuery(id+"F0.wireOp",EDGE,"E15.bottom");var subQ1=sQuery(id+"F0.wireOp",EDGE,"E14.right");var subQ2=makeQuery(id+"F0.imprint","INTERSECT",VERTEX,{"derivedFrom":[subQ1,subQ0]});Q59=makeQuery(id+"F0.imprint","IMPRINT",FACE,{"disambiguationData":[TD([[makeQuery(id+"F0.imprint","IMPRINT",EDGE,{"disambiguationData":[TD([[subQ2,-1.0]])],"derivedFrom":subQ1}),1.0]])]});}
            var Q60;
            {var subQ0=sQuery(id+"F0.wireOp",EDGE,"E36");Q60=makeQuery(id+"F0.imprint","IMPRINT",FACE,{"disambiguationData":[TD([[makeQuery(id+"F0.imprint","IMPRINT",EDGE,{"derivedFrom":subQ0}),-1.0]])]});}
            var Q61;
            {var subQ0=sQuery(id+"F0.wireOp",EDGE,"E47");var subQ1=sQuery(id+"F0.wireOp",EDGE,"E14.left");var subQ2=makeQuery(id+"F0.imprint","INTERSECT",VERTEX,{"derivedFrom":[subQ1,subQ0]});Q61=makeQuery(id+"F0.imprint","IMPRINT",FACE,{"disambiguationData":[TD([[makeQuery(id+"F0.imprint","IMPRINT",EDGE,{"disambiguationData":[TD([[subQ2,-1.0]])],"derivedFrom":subQ1}),-1.0]])]});}
            var Q62;
            {var subQ0=sQuery(id+"F0.wireOp",EDGE,"E37");Q62=makeQuery(id+"F0.imprint","IMPRINT",FACE,{"disambiguationData":[TD([[makeQuery(id+"F0.imprint","IMPRINT",EDGE,{"derivedFrom":subQ0}),1.0]])]});}
            var Q63;
            {var subQ0=sQuery(id+"F0.wireOp",EDGE,"E16.bottom");var subQ1=sQuery(id+"F0.wireOp",EDGE,"E14.left");var subQ2=makeQuery(id+"F0.imprint","INTERSECT",VERTEX,{"derivedFrom":[subQ1,subQ0]});Q63=makeQuery(id+"F0.imprint","IMPRINT",FACE,{"disambiguationData":[TD([[makeQuery(id+"F0.imprint","IMPRINT",EDGE,{"disambiguationData":[TD([[subQ2,-1.0]])],"derivedFrom":subQ1}),-1.0]])]});}
            var Q64;
            {var subQ0=sQuery(id+"F0.wireOp",EDGE,"E47");var subQ1=sQuery(id+"F0.wireOp",EDGE,"E14.left");var subQ2=makeQuery(id+"F0.imprint","INTERSECT",VERTEX,{"derivedFrom":[subQ1,subQ0]});Q64=makeQuery(id+"F0.imprint","IMPRINT",FACE,{"disambiguationData":[TD([[makeQuery(id+"F0.imprint","IMPRINT",EDGE,{"disambiguationData":[TD([[subQ2,-1.0]])],"derivedFrom":subQ1}),1.0]])]});}
            var Q65;
            {var subQ0=sQuery(id+"F0.wireOp",EDGE,"E16.top");var subQ1=sQuery(id+"F0.wireOp",EDGE,"E14.left");var subQ2=makeQuery(id+"F0.imprint","INTERSECT",VERTEX,{"derivedFrom":[subQ1,subQ0]});Q65=makeQuery(id+"F0.imprint","IMPRINT",FACE,{"disambiguationData":[TD([[makeQuery(id+"F0.imprint","IMPRINT",EDGE,{"disambiguationData":[TD([[subQ2,-1.0]])],"derivedFrom":subQ1}),1.0]])]});}
            var Q66;
            {var subQ0=sQuery(id+"F0.wireOp",EDGE,"E16.bottom");var subQ1=sQuery(id+"F0.wireOp",EDGE,"E14.left");var subQ2=makeQuery(id+"F0.imprint","INTERSECT",VERTEX,{"derivedFrom":[subQ1,subQ0]});Q66=makeQuery(id+"F0.imprint","IMPRINT",FACE,{"disambiguationData":[TD([[makeQuery(id+"F0.imprint","IMPRINT",EDGE,{"disambiguationData":[TD([[subQ2,-1.0]])],"derivedFrom":subQ1}),1.0]])]});}
            var Q67;
            {var subQ0=sQuery(id+"F0.wireOp",EDGE,"E16.bottom");var subQ1=sQuery(id+"F0.wireOp",EDGE,"E14.right");var subQ2=makeQuery(id+"F0.imprint","INTERSECT",VERTEX,{"derivedFrom":[subQ1,subQ0]});Q67=makeQuery(id+"F0.imprint","IMPRINT",FACE,{"disambiguationData":[TD([[makeQuery(id+"F0.imprint","IMPRINT",EDGE,{"disambiguationData":[TD([[subQ2,-1.0]])],"derivedFrom":subQ1}),1.0]])]});}
            var Q68;
            {var subQ0=sQuery(id+"F0.wireOp",EDGE,"E47");var subQ1=sQuery(id+"F0.wireOp",EDGE,"E14.right");var subQ2=makeQuery(id+"F0.imprint","INTERSECT",VERTEX,{"derivedFrom":[subQ1,subQ0]});Q68=makeQuery(id+"F0.imprint","IMPRINT",FACE,{"disambiguationData":[TD([[makeQuery(id+"F0.imprint","IMPRINT",EDGE,{"disambiguationData":[TD([[subQ2,-1.0]])],"derivedFrom":subQ1}),1.0]])]});}
            var Q69;
            {var subQ0=sQuery(id+"F0.wireOp",EDGE,"E38");Q69=makeQuery(id+"F0.imprint","IMPRINT",FACE,{"disambiguationData":[TD([[makeQuery(id+"F0.imprint","IMPRINT",EDGE,{"derivedFrom":subQ0}),-1.0]])]});}
            var Q70;
            {var subQ0=sQuery(id+"F0.wireOp",EDGE,"E17.top");var subQ1=sQuery(id+"F0.wireOp",EDGE,"E14.left");var subQ2=makeQuery(id+"F0.imprint","INTERSECT",VERTEX,{"derivedFrom":[subQ1,subQ0]});Q70=makeQuery(id+"F0.imprint","IMPRINT",FACE,{"disambiguationData":[TD([[makeQuery(id+"F0.imprint","IMPRINT",EDGE,{"disambiguationData":[TD([[subQ2,-1.0]])],"derivedFrom":subQ1}),1.0]])]});}
            var Q71;
            {var subQ0=sQuery(id+"F0.wireOp",EDGE,"E48");var subQ1=sQuery(id+"F0.wireOp",EDGE,"E14.left");var subQ2=makeQuery(id+"F0.imprint","INTERSECT",VERTEX,{"derivedFrom":[subQ1,subQ0]});Q71=makeQuery(id+"F0.imprint","IMPRINT",FACE,{"disambiguationData":[TD([[makeQuery(id+"F0.imprint","IMPRINT",EDGE,{"disambiguationData":[TD([[subQ2,-1.0]])],"derivedFrom":subQ1}),-1.0]])]});}
            var Q72;
            {var subQ0=sQuery(id+"F0.wireOp",EDGE,"E40");Q72=makeQuery(id+"F0.imprint","IMPRINT",FACE,{"disambiguationData":[TD([[makeQuery(id+"F0.imprint","IMPRINT",EDGE,{"derivedFrom":subQ0}),1.0]])]});}
            var Q73;
            {var subQ0=sQuery(id+"F0.wireOp",EDGE,"E17.bottom");var subQ1=sQuery(id+"F0.wireOp",EDGE,"E14.left");var subQ2=makeQuery(id+"F0.imprint","INTERSECT",VERTEX,{"derivedFrom":[subQ1,subQ0]});Q73=makeQuery(id+"F0.imprint","IMPRINT",FACE,{"disambiguationData":[TD([[makeQuery(id+"F0.imprint","IMPRINT",EDGE,{"disambiguationData":[TD([[subQ2,-1.0]])],"derivedFrom":subQ1}),-1.0]])]});}
            var Q74;
            {var subQ0=sQuery(id+"F0.wireOp",EDGE,"E17.bottom");var subQ1=sQuery(id+"F0.wireOp",EDGE,"E14.left");var subQ2=makeQuery(id+"F0.imprint","INTERSECT",VERTEX,{"derivedFrom":[subQ1,subQ0]});Q74=makeQuery(id+"F0.imprint","IMPRINT",FACE,{"disambiguationData":[TD([[makeQuery(id+"F0.imprint","IMPRINT",EDGE,{"disambiguationData":[TD([[subQ2,-1.0]])],"derivedFrom":subQ1}),1.0]])]});}
            var Q75;
            {var subQ0=sQuery(id+"F0.wireOp",EDGE,"E48");var subQ1=sQuery(id+"F0.wireOp",EDGE,"E14.right");var subQ2=makeQuery(id+"F0.imprint","INTERSECT",VERTEX,{"derivedFrom":[subQ1,subQ0]});Q75=makeQuery(id+"F0.imprint","IMPRINT",FACE,{"disambiguationData":[TD([[makeQuery(id+"F0.imprint","IMPRINT",EDGE,{"disambiguationData":[TD([[subQ2,-1.0]])],"derivedFrom":subQ1}),1.0]])]});}
            var Q76;
            {var subQ0=sQuery(id+"F0.wireOp",EDGE,"E17.bottom");var subQ1=sQuery(id+"F0.wireOp",EDGE,"E14.right");var subQ2=makeQuery(id+"F0.imprint","INTERSECT",VERTEX,{"derivedFrom":[subQ1,subQ0]});Q76=makeQuery(id+"F0.imprint","IMPRINT",FACE,{"disambiguationData":[TD([[makeQuery(id+"F0.imprint","IMPRINT",EDGE,{"disambiguationData":[TD([[subQ2,-1.0]])],"derivedFrom":subQ1}),1.0]])]});}
            var Q77;
            {var subQ0=sQuery(id+"F0.wireOp",EDGE,"E39");Q77=makeQuery(id+"F0.imprint","IMPRINT",FACE,{"disambiguationData":[TD([[makeQuery(id+"F0.imprint","IMPRINT",EDGE,{"derivedFrom":subQ0}),-1.0]])]});}
            var Q78;
            {var subQ0=sQuery(id+"F0.wireOp",EDGE,"E18.top");var subQ1=sQuery(id+"F0.wireOp",EDGE,"E14.left");var subQ2=makeQuery(id+"F0.imprint","INTERSECT",VERTEX,{"derivedFrom":[subQ1,subQ0]});Q78=makeQuery(id+"F0.imprint","IMPRINT",FACE,{"disambiguationData":[TD([[makeQuery(id+"F0.imprint","IMPRINT",EDGE,{"disambiguationData":[TD([[subQ2,-1.0]])],"derivedFrom":subQ1}),1.0]])]});}
            var Q79;
            {var subQ0=sQuery(id+"F0.wireOp",EDGE,"E49");var subQ1=sQuery(id+"F0.wireOp",EDGE,"E14.left");var subQ2=makeQuery(id+"F0.imprint","INTERSECT",VERTEX,{"derivedFrom":[subQ1,subQ0]});Q79=makeQuery(id+"F0.imprint","IMPRINT",FACE,{"disambiguationData":[TD([[makeQuery(id+"F0.imprint","IMPRINT",EDGE,{"disambiguationData":[TD([[subQ2,-1.0]])],"derivedFrom":subQ1}),1.0]])]});}
            var Q80;
            {var subQ4=sQuery(id+"F0.wireOp",EDGE,"E18.bottom");Q80=makeQuery(id+"F0.imprint","IMPRINT",FACE,{"disambiguationData":[TD([[makeQuery(id+"F0.imprint","IMPRINT",EDGE,{"derivedFrom":subQ4}),-1.0]])]});}
            var Q81;
            {var subQ0=sQuery(id+"F0.wireOp",EDGE,"E49");var subQ1=sQuery(id+"F0.wireOp",EDGE,"E14.left");var subQ2=makeQuery(id+"F0.imprint","INTERSECT",VERTEX,{"derivedFrom":[subQ1,subQ0]});Q81=makeQuery(id+"F0.imprint","IMPRINT",FACE,{"disambiguationData":[TD([[makeQuery(id+"F0.imprint","IMPRINT",EDGE,{"disambiguationData":[TD([[subQ2,-1.0]])],"derivedFrom":subQ1}),-1.0]])]});}
            var Q82;
            {var subQ0=sQuery(id+"F0.wireOp",EDGE,"E49");var subQ1=sQuery(id+"F0.wireOp",EDGE,"E14.right");var subQ2=makeQuery(id+"F0.imprint","INTERSECT",VERTEX,{"derivedFrom":[subQ1,subQ0]});Q82=makeQuery(id+"F0.imprint","IMPRINT",FACE,{"disambiguationData":[TD([[makeQuery(id+"F0.imprint","IMPRINT",EDGE,{"disambiguationData":[TD([[subQ2,-1.0]])],"derivedFrom":subQ1}),1.0]])]});}
            var Q83;
            {var subQ0=sQuery(id+"F0.wireOp",EDGE,"E48");var subQ1=sQuery(id+"F0.wireOp",EDGE,"E14.left");var subQ2=makeQuery(id+"F0.imprint","INTERSECT",VERTEX,{"derivedFrom":[subQ1,subQ0]});Q83=makeQuery(id+"F0.imprint","IMPRINT",FACE,{"disambiguationData":[TD([[makeQuery(id+"F0.imprint","IMPRINT",EDGE,{"disambiguationData":[TD([[subQ2,-1.0]])],"derivedFrom":subQ1}),1.0]])]});}
            var Q84;
            {var subQ0=sQuery(id+"F0.wireOp",EDGE,"E20.bottom");var subQ1=sQuery(id+"F0.wireOp",EDGE,"E14.right");var subQ2=makeQuery(id+"F0.imprint","INTERSECT",VERTEX,{"derivedFrom":[subQ1,subQ0]});Q84=makeQuery(id+"F0.imprint","IMPRINT",FACE,{"disambiguationData":[TD([[makeQuery(id+"F0.imprint","IMPRINT",EDGE,{"disambiguationData":[TD([[subQ2,-1.0]])],"derivedFrom":subQ1}),1.0]])]});}
            extrude(context, id + "F4", {"entities" : qUnion([Q0, Q1, Q2, Q3, Q4, Q5, Q6, Q7, Q8, Q9, Q10, Q11, Q12, Q13, Q14, Q15, Q16, Q17, Q18, Q19, Q20, Q21, Q22, Q23, Q24, Q25, Q26, Q27, Q28, Q29, Q30, Q31, Q32, Q33, Q34, Q35, Q36, Q37, Q38, Q39, Q40, Q41, Q42, Q43, Q44, Q45, Q46, Q47, Q48, Q49, Q50, Q51, Q52, Q53, Q54, Q55, Q56, Q57, Q58, Q59, Q60, Q61, Q62, Q63, Q64, Q65, Q66, Q67, Q68, Q69, Q70, Q71, Q72, Q73, Q74, Q75, Q76, Q77, Q78, Q79, Q80, Q81, Q82, Q83, Q84]), "depth" : 9.52 * mm, "offsetDistance" : 25.4 * mm});
        }
    });
